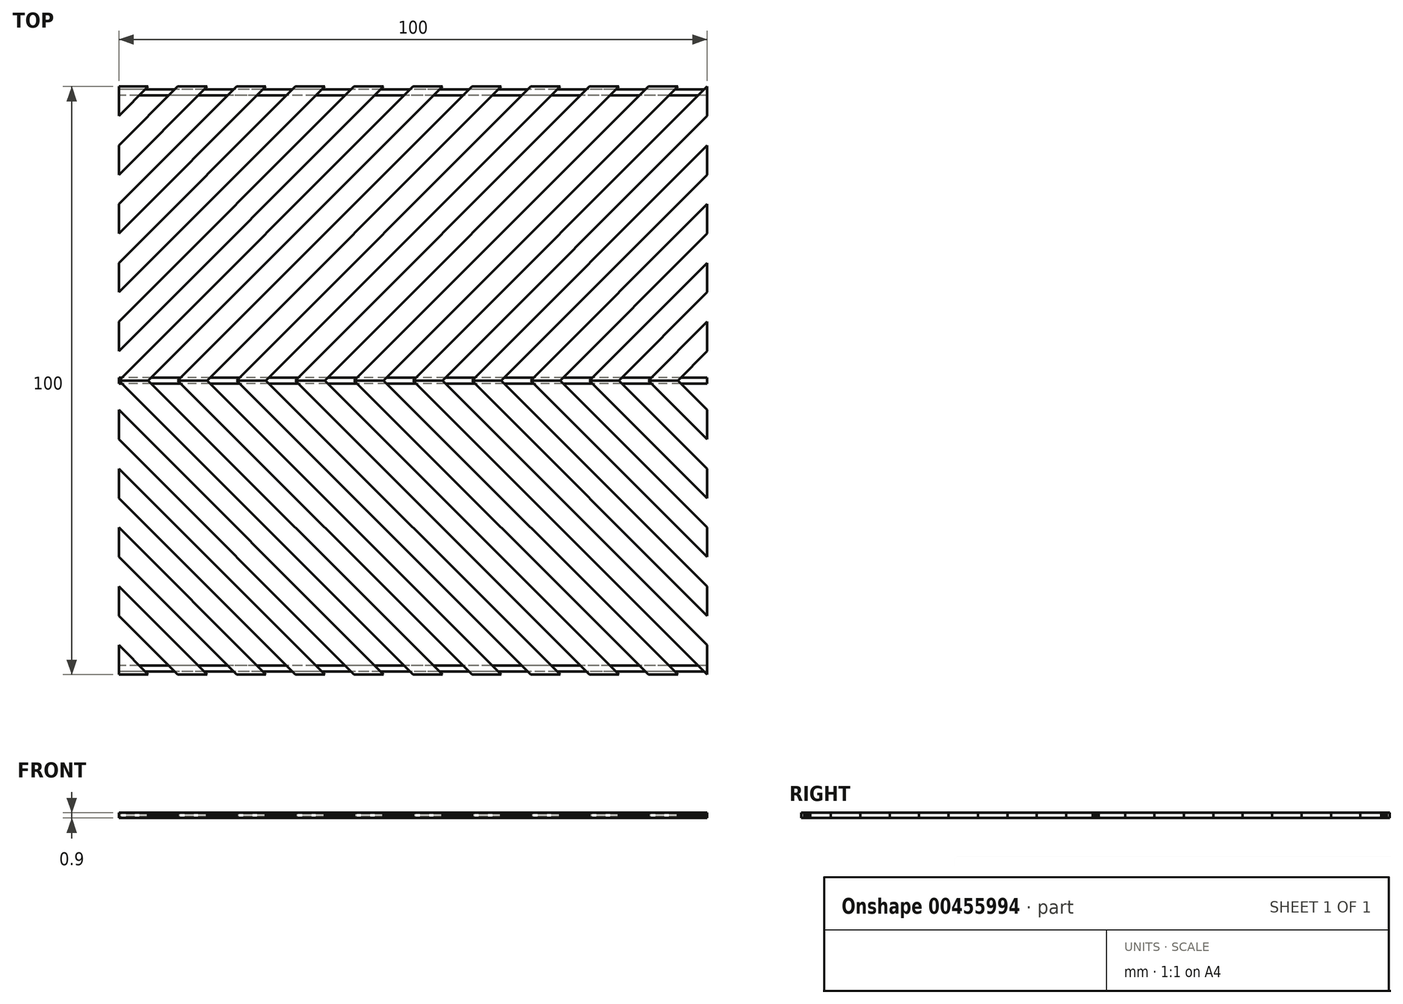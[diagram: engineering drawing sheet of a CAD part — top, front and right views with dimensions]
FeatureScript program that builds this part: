
annotation { "Feature Type Name" : "Feature", "Feature Type Description" : "" }
export const myFeature = defineFeature(function(context is Context, id is Id, definition is map)
    precondition{}
    {
        {
            var Q0;
            Q0=qCreatedBy(makeId("Top.planeOp"),FACE);
            var sketch = newSketch(context, id + "F0", { "sketchPlane" : qUnion([Q0])});
            skLineSegment(sketch, "E0.bottom", {"start": v(50, -50) * mm, "end": v(-50, -50) * mm});
            skLineSegment(sketch, "E0.top", {"start": v(50, 50) * mm, "end": v(-50, 50) * mm});
            skLineSegment(sketch, "E0.left", {"start": v(50, -50) * mm, "end": v(50, 50) * mm});
            skLineSegment(sketch, "E0.right", {"start": v(-50, -50) * mm, "end": v(-50, 50) * mm});
            skPoint(sketch, "E0.middle", {"position": v(0, 0) * mm});
            skLineSegment(sketch, "E1", {"start": v(-50, 0) * mm, "end": v(0, 50) * mm});
            skLineSegment(sketch, "E2", {"start": v(0, 50) * mm, "end": v(5, 50) * mm});
            skLineSegment(sketch, "E3", {"start": v(5, 50) * mm, "end": v(-45, 0) * mm});
            skLineSegment(sketch, "E4", {"start": v(-45, 0) * mm, "end": v(-50, 0) * mm});
            skLineSegment(sketch, "E5", {"start": v(-5, 50) * mm, "end": v(-50, 5) * mm});
            skLineSegment(sketch, "E6", {"start": v(-50, 5) * mm, "end": v(-50, 10) * mm});
            skLineSegment(sketch, "E7", {"start": v(-50, 10) * mm, "end": v(-10, 50) * mm});
            skLineSegment(sketch, "E8", {"start": v(-10, 50) * mm, "end": v(-5, 50) * mm});
            skLineSegment(sketch, "E9", {"start": v(-50, 15) * mm, "end": v(-15, 50) * mm});
            skLineSegment(sketch, "E10", {"start": v(-50, 20) * mm, "end": v(-20, 50) * mm});
            skLineSegment(sketch, "E11", {"start": v(-40, 0) * mm, "end": v(10, 50) * mm});
            skLineSegment(sketch, "E12", {"start": v(10, 50) * mm, "end": v(15, 50) * mm});
            skLineSegment(sketch, "E13", {"start": v(15, 50) * mm, "end": v(-35, 0) * mm});
            skLineSegment(sketch, "E14", {"start": v(-35, 0) * mm, "end": v(-40, 0) * mm});
            skLineSegment(sketch, "E15", {"start": v(-30, 0) * mm, "end": v(20, 50) * mm});
            skLineSegment(sketch, "E16", {"start": v(20, 50) * mm, "end": v(25, 50) * mm});
            skLineSegment(sketch, "E17", {"start": v(25, 50) * mm, "end": v(-25, 0) * mm});
            skLineSegment(sketch, "E18", {"start": v(-25, 0) * mm, "end": v(-30, 0) * mm});
            skLineSegment(sketch, "E19", {"start": v(-20, 0) * mm, "end": v(30, 50) * mm});
            skLineSegment(sketch, "E20", {"start": v(30, 50) * mm, "end": v(35, 50) * mm});
            skLineSegment(sketch, "E21", {"start": v(35, 50) * mm, "end": v(-15, 0) * mm});
            skLineSegment(sketch, "E22", {"start": v(-15, 0) * mm, "end": v(-20, 0) * mm});
            skLineSegment(sketch, "E23", {"start": v(-10, 0) * mm, "end": v(40, 50) * mm});
            skLineSegment(sketch, "E24", {"start": v(40, 50) * mm, "end": v(45, 50) * mm});
            skLineSegment(sketch, "E25", {"start": v(45, 50) * mm, "end": v(-5, 0) * mm});
            skLineSegment(sketch, "E26", {"start": v(-5, 0) * mm, "end": v(-10, 0) * mm});
            skLineSegment(sketch, "E27", {"start": v(0, 0) * mm, "end": v(50, 50) * mm});
            skLineSegment(sketch, "E28", {"start": v(0, 0) * mm, "end": v(5, 0) * mm});
            skLineSegment(sketch, "E29", {"start": v(5, 0) * mm, "end": v(50, 45) * mm});
            skLineSegment(sketch, "E30", {"start": v(50, 45) * mm, "end": v(50, 50) * mm});
            skLineSegment(sketch, "E31", {"start": v(10, 0) * mm, "end": v(50, 40) * mm});
            skLineSegment(sketch, "E32", {"start": v(50, 40) * mm, "end": v(50, 35) * mm});
            skLineSegment(sketch, "E33", {"start": v(50, 35) * mm, "end": v(15, 0) * mm});
            skLineSegment(sketch, "E34", {"start": v(15, 0) * mm, "end": v(10, 0) * mm});
            skLineSegment(sketch, "E35", {"start": v(20, 0) * mm, "end": v(50, 30) * mm});
            skLineSegment(sketch, "E36", {"start": v(50, 30) * mm, "end": v(50, 25) * mm});
            skLineSegment(sketch, "E37", {"start": v(50, 25) * mm, "end": v(25, 0) * mm});
            skLineSegment(sketch, "E38", {"start": v(25, 0) * mm, "end": v(20, 0) * mm});
            skLineSegment(sketch, "E39", {"start": v(-50, 25) * mm, "end": v(-25, 50) * mm});
            skLineSegment(sketch, "E40", {"start": v(-25, 50) * mm, "end": v(-30, 50) * mm});
            skLineSegment(sketch, "E41", {"start": v(-30, 50) * mm, "end": v(-50, 30) * mm});
            skLineSegment(sketch, "E42", {"start": v(-50, 30) * mm, "end": v(-50, 25) * mm});
            skLineSegment(sketch, "E43", {"start": v(-35, 50) * mm, "end": v(-50, 35) * mm});
            skLineSegment(sketch, "E44", {"start": v(-50, 35) * mm, "end": v(-50, 40) * mm});
            skLineSegment(sketch, "E45", {"start": v(-50, 40) * mm, "end": v(-40, 50) * mm});
            skLineSegment(sketch, "E46", {"start": v(-40, 50) * mm, "end": v(-35, 50) * mm});
            skLineSegment(sketch, "E47", {"start": v(30, 0) * mm, "end": v(50, 20) * mm});
            skLineSegment(sketch, "E48", {"start": v(50, 20) * mm, "end": v(50, 15) * mm});
            skLineSegment(sketch, "E49", {"start": v(50, 15) * mm, "end": v(35, 0) * mm});
            skLineSegment(sketch, "E50", {"start": v(35, 0) * mm, "end": v(30, 0) * mm});
            skLineSegment(sketch, "E51", {"start": v(-50, 45) * mm, "end": v(-45, 50) * mm});
            skLineSegment(sketch, "E52", {"start": v(50, 10) * mm, "end": v(40, 0) * mm});
            skPoint(sketch, "E52.endSnap0", {"position": v(32.5, 0) * mm});
            skLineSegment(sketch, "E53", {"start": v(40, 0) * mm, "end": v(45, 0) * mm});
            skLineSegment(sketch, "E54", {"start": v(45, 0) * mm, "end": v(50, 5) * mm});
            skLineSegment(sketch, "E55", {"start": v(50, 5) * mm, "end": v(50, 10) * mm});
            skSolve(sketch);
        }
        {
            var Q0;
            {var subQ0=sQuery(id+"F0.wireOp",EDGE,"E9");Q0=makeQuery(id+"F0.imprint","IMPRINT",FACE,{"disambiguationData":[TD([[makeQuery(id+"F0.imprint","IMPRINT",EDGE,{"derivedFrom":subQ0}),1.0]])]});}
            var Q1;
            Q1=makeQuery(id+"F0.imprint","IMPRINT",FACE,{"disambiguationData":[TD([[makeQuery(id+"F0.imprint","IMPRINT",EDGE,{"derivedFrom":sQuery(id+"F0.wireOp",EDGE,"E5")}),-1.0]])]});
            var Q2;
            Q2=makeQuery(id+"F0.imprint","IMPRINT",FACE,{"disambiguationData":[TD([[makeQuery(id+"F0.imprint","IMPRINT",EDGE,{"derivedFrom":sQuery(id+"F0.wireOp",EDGE,"E1")}),-1.0]])]});
            var Q3;
            Q3=makeQuery(id+"F0.imprint","IMPRINT",FACE,{"disambiguationData":[TD([[makeQuery(id+"F0.imprint","IMPRINT",EDGE,{"derivedFrom":sQuery(id+"F0.wireOp",EDGE,"E11")}),-1.0]])]});
            var Q4;
            Q4=makeQuery(id+"F0.imprint","IMPRINT",FACE,{"disambiguationData":[TD([[makeQuery(id+"F0.imprint","IMPRINT",EDGE,{"derivedFrom":sQuery(id+"F0.wireOp",EDGE,"E15")}),-1.0]])]});
            var Q5;
            Q5=makeQuery(id+"F0.imprint","IMPRINT",FACE,{"disambiguationData":[TD([[makeQuery(id+"F0.imprint","IMPRINT",EDGE,{"derivedFrom":sQuery(id+"F0.wireOp",EDGE,"E19")}),-1.0]])]});
            var Q6;
            Q6=makeQuery(id+"F0.imprint","IMPRINT",FACE,{"disambiguationData":[TD([[makeQuery(id+"F0.imprint","IMPRINT",EDGE,{"derivedFrom":sQuery(id+"F0.wireOp",EDGE,"E23")}),-1.0]])]});
            var Q7;
            Q7=makeQuery(id+"F0.imprint","IMPRINT",FACE,{"disambiguationData":[TD([[makeQuery(id+"F0.imprint","IMPRINT",EDGE,{"derivedFrom":sQuery(id+"F0.wireOp",EDGE,"E27")}),-1.0]])]});
            var Q8;
            Q8=makeQuery(id+"F0.imprint","IMPRINT",FACE,{"disambiguationData":[TD([[makeQuery(id+"F0.imprint","IMPRINT",EDGE,{"derivedFrom":sQuery(id+"F0.wireOp",EDGE,"E31")}),-1.0]])]});
            var Q9;
            Q9=makeQuery(id+"F0.imprint","IMPRINT",FACE,{"disambiguationData":[TD([[makeQuery(id+"F0.imprint","IMPRINT",EDGE,{"derivedFrom":sQuery(id+"F0.wireOp",EDGE,"E35")}),-1.0]])]});
            var Q10;
            Q10=makeQuery(id+"F0.imprint","IMPRINT",FACE,{"disambiguationData":[TD([[makeQuery(id+"F0.imprint","IMPRINT",EDGE,{"derivedFrom":sQuery(id+"F0.wireOp",EDGE,"E39")}),1.0]])]});
            var Q11;
            Q11=makeQuery(id+"F0.imprint","IMPRINT",FACE,{"disambiguationData":[TD([[makeQuery(id+"F0.imprint","IMPRINT",EDGE,{"derivedFrom":sQuery(id+"F0.wireOp",EDGE,"E43")}),-1.0]])]});
            var Q12;
            {var subQ3=sQuery(id+"F0.wireOp",EDGE,"E51");Q12=makeQuery(id+"F0.imprint","IMPRINT",FACE,{"disambiguationData":[TD([[makeQuery(id+"F0.imprint","IMPRINT",EDGE,{"derivedFrom":subQ3}),1.0]])]});}
            var Q13;
            Q13=makeQuery(id+"F0.imprint","IMPRINT",FACE,{"disambiguationData":[TD([[makeQuery(id+"F0.imprint","IMPRINT",EDGE,{"derivedFrom":sQuery(id+"F0.wireOp",EDGE,"E47")}),-1.0]])]});
            var Q14;
            Q14=makeQuery(id+"F0.imprint","IMPRINT",FACE,{"disambiguationData":[TD([[makeQuery(id+"F0.imprint","IMPRINT",EDGE,{"derivedFrom":sQuery(id+"F0.wireOp",EDGE,"E52")}),1.0]])]});
            extrude(context, id + "F1", {"entities" : qUnion([Q0, Q1, Q2, Q3, Q4, Q5, Q6, Q7, Q8, Q9, Q10, Q11, Q12, Q13, Q14]), "endBound" : BoundingType.SYMMETRIC, "depth" : 0.9 * mm});
        }
        {
            var Q0;
            Q0=makeQuery(id+"F1.opExtrude","SWEPT_BODY",BODY,{"disambiguationData":[OSD([sQuery(id+"F0.wireOp",EDGE,"E0.top"),sQuery(id+"F0.wireOp",EDGE,"E0.right"),sQuery(id+"F0.wireOp",EDGE,"E9"),sQuery(id+"F0.wireOp",EDGE,"E10")])]});
            var Q1;
            Q1=makeQuery(id+"F1.opExtrude","SWEPT_BODY",BODY,{"disambiguationData":[OSD([sQuery(id+"F0.wireOp",EDGE,"E0.top"),sQuery(id+"F0.wireOp",EDGE,"E0.right"),sQuery(id+"F0.wireOp",EDGE,"E51")])]});
            var Q2;
            Q2=makeQuery(id+"F1.opExtrude","SWEPT_BODY",BODY,{"disambiguationData":[OSD([sQuery(id+"F0.wireOp",EDGE,"E1"),sQuery(id+"F0.wireOp",EDGE,"E2"),sQuery(id+"F0.wireOp",EDGE,"E3"),sQuery(id+"F0.wireOp",EDGE,"E4")])]});
            var Q3;
            Q3=makeQuery(id+"F1.opExtrude","SWEPT_BODY",BODY,{"disambiguationData":[OSD([sQuery(id+"F0.wireOp",EDGE,"E5"),sQuery(id+"F0.wireOp",EDGE,"E6"),sQuery(id+"F0.wireOp",EDGE,"E7"),sQuery(id+"F0.wireOp",EDGE,"E8")])]});
            var Q4;
            Q4=makeQuery(id+"F1.opExtrude","SWEPT_BODY",BODY,{"disambiguationData":[OSD([sQuery(id+"F0.wireOp",EDGE,"E11"),sQuery(id+"F0.wireOp",EDGE,"E12"),sQuery(id+"F0.wireOp",EDGE,"E13"),sQuery(id+"F0.wireOp",EDGE,"E14")])]});
            var Q5;
            Q5=makeQuery(id+"F1.opExtrude","SWEPT_BODY",BODY,{"disambiguationData":[OSD([sQuery(id+"F0.wireOp",EDGE,"E15"),sQuery(id+"F0.wireOp",EDGE,"E16"),sQuery(id+"F0.wireOp",EDGE,"E17"),sQuery(id+"F0.wireOp",EDGE,"E18")])]});
            var Q6;
            Q6=makeQuery(id+"F1.opExtrude","SWEPT_BODY",BODY,{"disambiguationData":[OSD([sQuery(id+"F0.wireOp",EDGE,"E19"),sQuery(id+"F0.wireOp",EDGE,"E20"),sQuery(id+"F0.wireOp",EDGE,"E21"),sQuery(id+"F0.wireOp",EDGE,"E22")])]});
            var Q7;
            Q7=makeQuery(id+"F1.opExtrude","SWEPT_BODY",BODY,{"disambiguationData":[OSD([sQuery(id+"F0.wireOp",EDGE,"E23"),sQuery(id+"F0.wireOp",EDGE,"E24"),sQuery(id+"F0.wireOp",EDGE,"E25"),sQuery(id+"F0.wireOp",EDGE,"E26")])]});
            var Q8;
            Q8=makeQuery(id+"F1.opExtrude","SWEPT_BODY",BODY,{"disambiguationData":[OSD([sQuery(id+"F0.wireOp",EDGE,"E27"),sQuery(id+"F0.wireOp",EDGE,"E28"),sQuery(id+"F0.wireOp",EDGE,"E29"),sQuery(id+"F0.wireOp",EDGE,"E30")])]});
            var Q9;
            Q9=makeQuery(id+"F1.opExtrude","SWEPT_BODY",BODY,{"disambiguationData":[OSD([sQuery(id+"F0.wireOp",EDGE,"E31"),sQuery(id+"F0.wireOp",EDGE,"E32"),sQuery(id+"F0.wireOp",EDGE,"E33"),sQuery(id+"F0.wireOp",EDGE,"E34")])]});
            var Q10;
            Q10=makeQuery(id+"F1.opExtrude","SWEPT_BODY",BODY,{"disambiguationData":[OSD([sQuery(id+"F0.wireOp",EDGE,"E35"),sQuery(id+"F0.wireOp",EDGE,"E36"),sQuery(id+"F0.wireOp",EDGE,"E37"),sQuery(id+"F0.wireOp",EDGE,"E38")])]});
            var Q11;
            Q11=makeQuery(id+"F1.opExtrude","SWEPT_BODY",BODY,{"disambiguationData":[OSD([sQuery(id+"F0.wireOp",EDGE,"E39"),sQuery(id+"F0.wireOp",EDGE,"E40"),sQuery(id+"F0.wireOp",EDGE,"E41"),sQuery(id+"F0.wireOp",EDGE,"E42")])]});
            var Q12;
            Q12=makeQuery(id+"F1.opExtrude","SWEPT_BODY",BODY,{"disambiguationData":[OSD([sQuery(id+"F0.wireOp",EDGE,"E43"),sQuery(id+"F0.wireOp",EDGE,"E44"),sQuery(id+"F0.wireOp",EDGE,"E45"),sQuery(id+"F0.wireOp",EDGE,"E46")])]});
            var Q13;
            Q13=makeQuery(id+"F1.opExtrude","SWEPT_BODY",BODY,{"disambiguationData":[OSD([sQuery(id+"F0.wireOp",EDGE,"E47"),sQuery(id+"F0.wireOp",EDGE,"E48"),sQuery(id+"F0.wireOp",EDGE,"E49"),sQuery(id+"F0.wireOp",EDGE,"E50")])]});
            var Q14;
            Q14=makeQuery(id+"F1.opExtrude","SWEPT_BODY",BODY,{"disambiguationData":[OSD([sQuery(id+"F0.wireOp",EDGE,"E52"),sQuery(id+"F0.wireOp",EDGE,"E53"),sQuery(id+"F0.wireOp",EDGE,"E54"),sQuery(id+"F0.wireOp",EDGE,"E55")])]});
            var Q15;
            Q15=qCreatedBy(makeId("Front.planeOp"),FACE);
            mirror(context, id + "F2", {"entities" : qUnion([Q0, Q1, Q2, Q3, Q4, Q5, Q6, Q7, Q8, Q9, Q10, Q11, Q12, Q13, Q14]), "mirrorPlane" : qUnion([Q15])});
        }
        {
            var Q0;
            Q0=qCreatedBy(makeId("Top.planeOp"),FACE);
            var sketch = newSketch(context, id + "F3", { "sketchPlane" : qUnion([Q0])});
            skLineSegment(sketch, "E56.bottom", {"start": v(50, 48.5) * mm, "end": v(-50, 48.5) * mm});
            skLineSegment(sketch, "E56.top", {"start": v(50, 49.5) * mm, "end": v(-50, 49.5) * mm});
            skLineSegment(sketch, "E56.left", {"start": v(50, 48.5) * mm, "end": v(50, 49.5) * mm});
            skLineSegment(sketch, "E56.right", {"start": v(-50, 48.5) * mm, "end": v(-50, 49.5) * mm});
            skPoint(sketch, "E56.middle", {"position": v(0, 49) * mm});
            skLineSegment(sketch, "E57.bottom", {"start": v(50, -48.5) * mm, "end": v(-50, -48.5) * mm});
            skLineSegment(sketch, "E57.top", {"start": v(50, -49.5) * mm, "end": v(-50, -49.5) * mm});
            skLineSegment(sketch, "E57.left", {"start": v(50, -48.5) * mm, "end": v(50, -49.5) * mm});
            skLineSegment(sketch, "E57.right", {"start": v(-50, -48.5) * mm, "end": v(-50, -49.5) * mm});
            skPoint(sketch, "E57.middle", {"position": v(0, -49) * mm});
            skLineSegment(sketch, "E58.bottom", {"start": v(50, -0.5) * mm, "end": v(-50, -0.5) * mm});
            skLineSegment(sketch, "E58.top", {"start": v(50, 0.5) * mm, "end": v(-50, 0.5) * mm});
            skLineSegment(sketch, "E58.left", {"start": v(50, -0.5) * mm, "end": v(50, 0.5) * mm});
            skLineSegment(sketch, "E58.right", {"start": v(-50, -0.5) * mm, "end": v(-50, 0.5) * mm});
            skPoint(sketch, "E58.middle", {"position": v(0, 0) * mm});
            skSolve(sketch);
        }
        {
            var Q0;
            Q0=makeQuery(id+"F3.imprint","IMPRINT",FACE,{"disambiguationData":[TD([[makeQuery(id+"F3.imprint","IMPRINT",EDGE,{"derivedFrom":sQuery(id+"F3.wireOp",EDGE,"E56.bottom")}),-1.0]])]});
            var Q1;
            Q1=makeQuery(id+"F3.imprint","IMPRINT",FACE,{"disambiguationData":[TD([[makeQuery(id+"F3.imprint","IMPRINT",EDGE,{"derivedFrom":sQuery(id+"F3.wireOp",EDGE,"E57.bottom")}),1.0]])]});
            var Q2;
            Q2=makeQuery(id+"F3.imprint","IMPRINT",FACE,{"disambiguationData":[TD([[makeQuery(id+"F3.imprint","IMPRINT",EDGE,{"derivedFrom":sQuery(id+"F3.wireOp",EDGE,"E58.bottom")}),-1.0]])]});
            extrude(context, id + "F4", {"entities" : qUnion([Q0, Q1, Q2]), "endBound" : BoundingType.SYMMETRIC, "depth" : 0.4 * mm});
        }
    });
